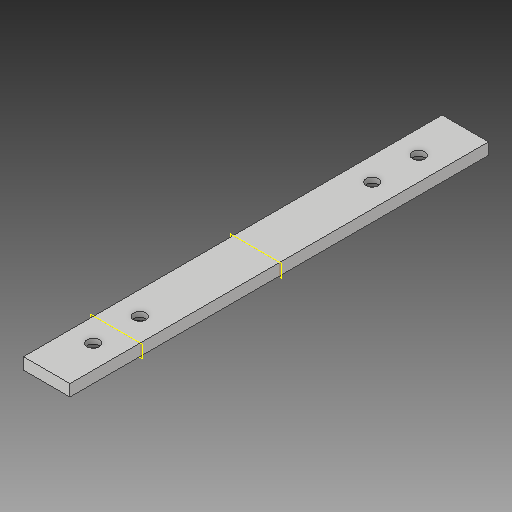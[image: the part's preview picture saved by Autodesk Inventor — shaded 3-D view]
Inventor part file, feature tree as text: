
AUTODESK INVENTOR PART (.ipt)
format: ipt  version: 2019 (Build 230136000, 136)  size: 118,272 bytes
history: native  units: in
note: dims shown in document units (in); Inventor stores cm internally (conversion verified against a paired STEP export)
features: extrude x3, sketch x3, mirror x2, plane x1
ambient origin geometry x8: Origin, YZ Plane, XZ Plane, XY Plane, X Axis, Y Axis, Z Axis, Center Point
bodies: Solid1 (feature_tree)
feature tree (9):
  extrude  "Extrusion1"  Depth=9.0in
  extrude  "Extrusion2"  Depth=0.25in
  extrude  "Extrusion3"  Depth=0.14in TaperAngle=0.0deg
  plane  "Work Plane2"
  mirror  "Mirror1"
  mirror  "Mirror2"
  sketch  "Sketch1"  dims[d0=1.0in d1=9.0in]
  sketch  "Sketch3"  dims[d2=0.25in d3=0.0in d5=0.5in]
  sketch  "Sketch4"  dims[d6=2.0in d7=0.14in d8=0.0in d9=0.266in d10=0.14in d11=0.0in d13=-1.5in]
